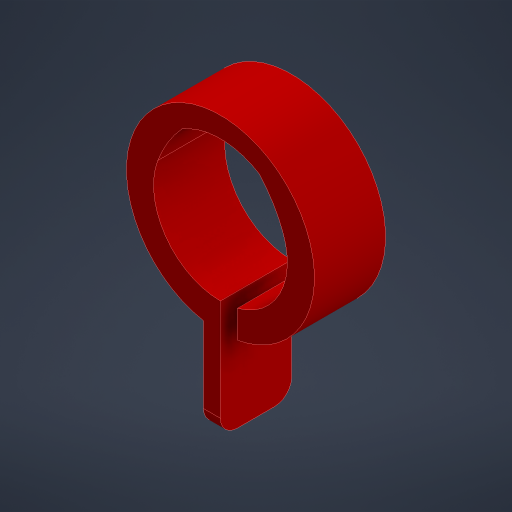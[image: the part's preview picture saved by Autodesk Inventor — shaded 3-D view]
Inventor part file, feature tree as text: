
AUTODESK INVENTOR PART (.ipt)
format: ipt  version: 2023.4 (Build 274418000, 418)  size: 255,488 bytes
history: native  units: mm
features: extrude x5, fillet x2, sketch x1
ambient origin geometry x8: Origin, YZ Plane, XZ Plane, XY Plane, X Axis, Y Axis, Z Axis, Center Point
bodies: Solid1 (feature_tree)
feature tree (8):
  sketch  "Sketch1"  dims[d0=19.75mm d1=3.0mm d3=2.5mm d4=10.0mm d5=1.25mm d6=2.5mm d7=1.0mm d8=2.5mm d9=0.0mm d10=5.5mm d11=0.0mm d12=2.5mm d13=0.0mm d14=2.5mm d15=17.5mm d16=9.25mm d17=9.25mm d18=2.5mm d19=1.0mm d20=2.5mm d21=0.0mm d22=2.5mm d23=17.5mm d24=2.5mm d25=10.0mm d26=0.0mm]
  extrude  "Extrusion1"  Depth=10.0mm
  extrude  "Extrusion2"  Depth=2.5mm
  extrude  "Extrusion3"  Depth=10.0mm
  fillet  "Fillet1"  Radius=1.25mm
  extrude  "Extrusion4"  Depth=2.5mm
  extrude  "Extrusion5"  Depth=10.0mm
  fillet  "Fillet2"  Radius=2.5mm
